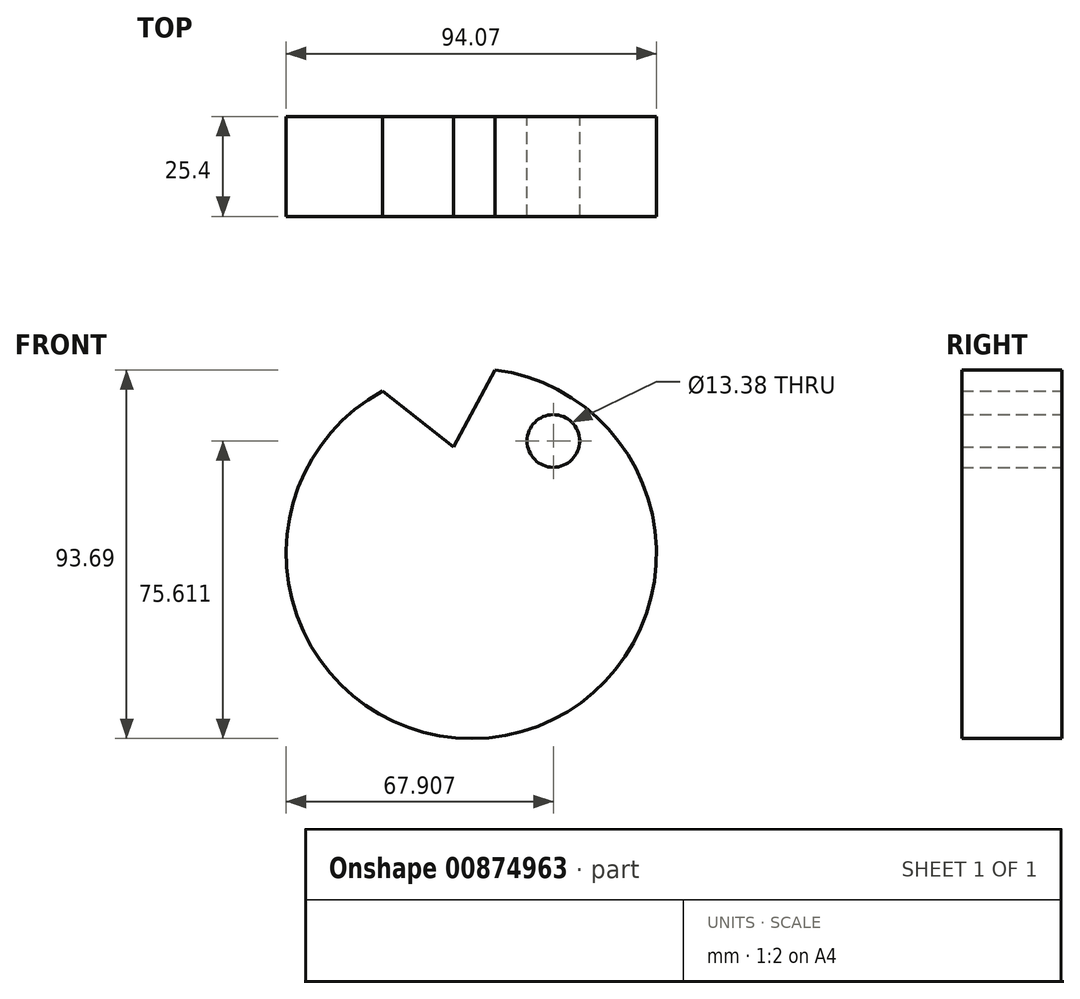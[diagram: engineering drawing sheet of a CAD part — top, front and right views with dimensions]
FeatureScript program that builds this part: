
annotation { "Feature Type Name" : "Feature", "Feature Type Description" : "" }
export const myFeature = defineFeature(function(context is Context, id is Id, definition is map)
    precondition{}
    {
        {
            var Q0;
            Q0=qCreatedBy(makeId("Front.planeOp"),FACE);
            var sketch = newSketch(context, id + "F0", { "sketchPlane" : qUnion([Q0])});
            skArc(sketch, "E0", {"start": v(-9.1, 17.37) * mm, "mid": v(22.2, -70.1) * mm, "end": v(19.43, 22.77) * mm});
            skLineSegment(sketch, "E1", {"start": v(-9.1, 17.37) * mm, "end": v(8.97, 3.1) * mm});
            skLineSegment(sketch, "E2", {"start": v(8.97, 3.1) * mm, "end": v(19.43, 22.77) * mm});
            skCircle(sketch, "E3", {"center": v(34.34, 4.7) * mm, "radius": 6.69 * mm});
            skSolve(sketch);
        }
        {
            var Q0;
            Q0 = qSketchRegion(id + "F0", true);
            extrude(context, id + "F1", {"entities" : qUnion([Q0]), "depth" : 25.4 * mm, "offsetDistance" : 25.4 * mm});
        }
    });
